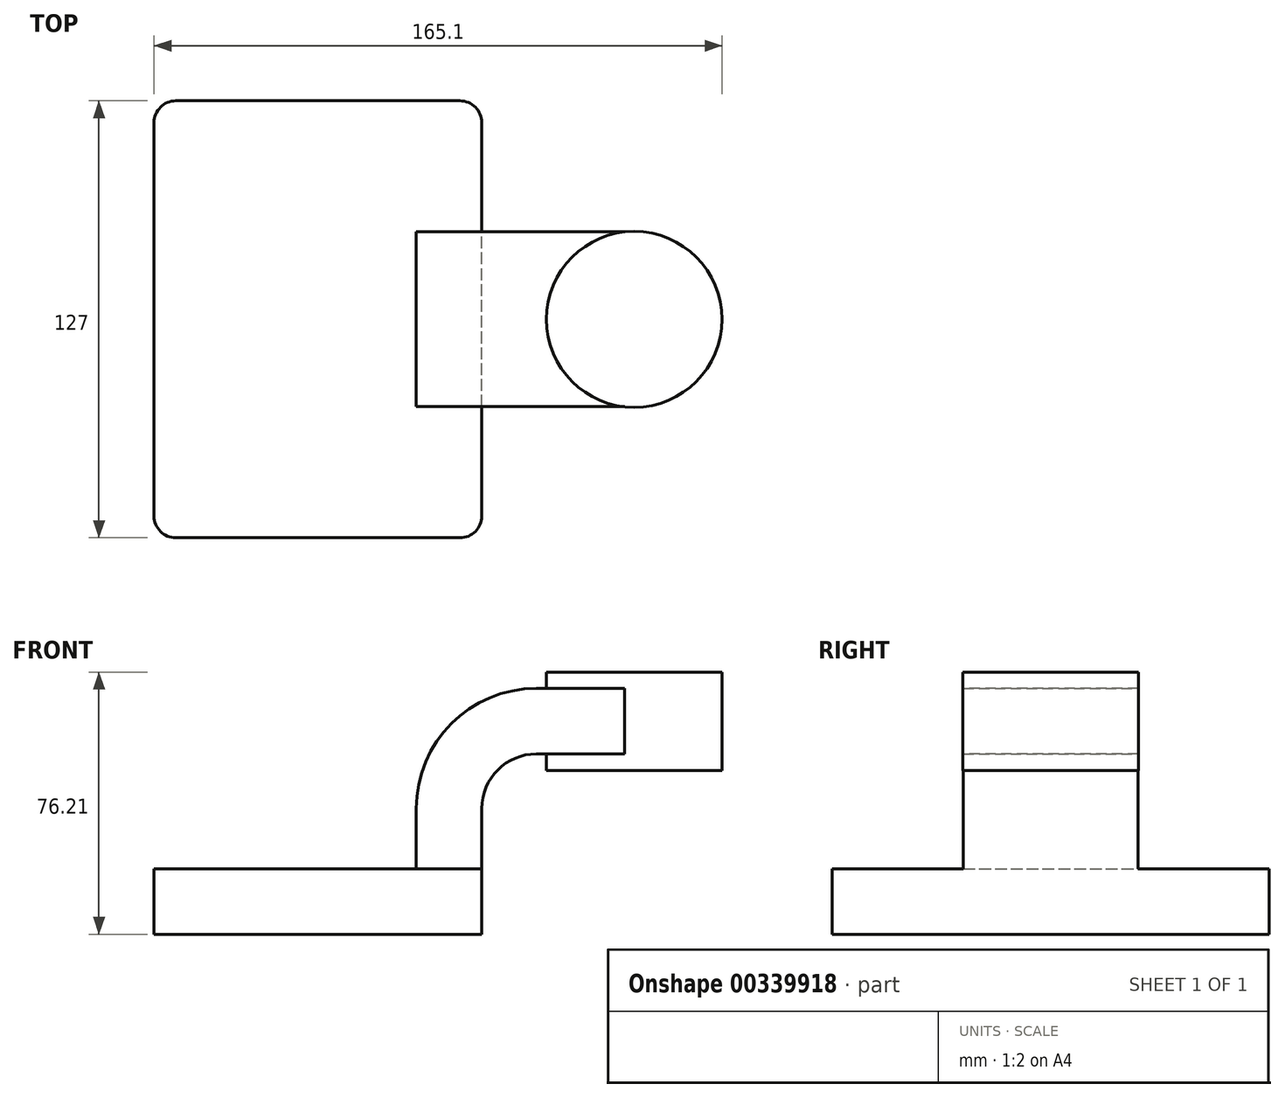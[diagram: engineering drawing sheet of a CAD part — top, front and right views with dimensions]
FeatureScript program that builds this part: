
annotation { "Feature Type Name" : "Feature", "Feature Type Description" : "" }
export const myFeature = defineFeature(function(context is Context, id is Id, definition is map)
    precondition{}
    {
        {
            var Q0;
            Q0=qCreatedBy(makeId("Front.planeOp"),FACE);
            var sketch = newSketch(context, id + "F0", { "sketchPlane" : qUnion([Q0])});
            skLineSegment(sketch, "E0.bottom", {"start": v(-47.63, 9.53) * mm, "end": v(47.63, 9.53) * mm});
            skLineSegment(sketch, "E0.top", {"start": v(-47.63, -9.53) * mm, "end": v(47.63, -9.53) * mm});
            skLineSegment(sketch, "E0.left", {"start": v(-47.63, 9.53) * mm, "end": v(-47.63, -9.53) * mm});
            skLineSegment(sketch, "E0.right", {"start": v(47.63, 9.53) * mm, "end": v(47.63, -9.53) * mm});
            skPoint(sketch, "E0.middle", {"position": v(0, 0) * mm});
            skLineSegment(sketch, "E1", {"start": v(47.63, 9.53) * mm, "end": v(47.63, 27) * mm});
            skArc(sketch, "E2", {"start": v(47.63, 27) * mm, "mid": v(52.27, 38.23) * mm, "end": v(63.5, 42.88) * mm});
            skLineSegment(sketch, "E3", {"start": v(63.5, 42.88) * mm, "end": v(91.92, 42.88) * mm});
            skLineSegment(sketch, "E4.bottom", {"start": v(117.47, 38.1) * mm, "end": v(66.67, 38.1) * mm});
            skLineSegment(sketch, "E4.top", {"start": v(117.47, 66.68) * mm, "end": v(66.67, 66.68) * mm});
            skLineSegment(sketch, "E4.left", {"start": v(117.47, 38.1) * mm, "end": v(117.47, 66.68) * mm});
            skLineSegment(sketch, "E4.right", {"start": v(66.67, 38.1) * mm, "end": v(66.67, 66.68) * mm});
            skPoint(sketch, "E4.middle", {"position": v(92.07, 52.39) * mm});
            skLineSegment(sketch, "E5.0", {"start": v(63.5, 61.93) * mm, "end": v(91.92, 61.93) * mm});
            skArc(sketch, "E5.1", {"start": v(28.58, 27) * mm, "mid": v(38.8, 51.7) * mm, "end": v(63.5, 61.93) * mm});
            skLineSegment(sketch, "E5.2", {"start": v(28.58, 9.53) * mm, "end": v(28.58, 27) * mm});
            skFitSpline(sketch, "E6", {"points": [v(-47.63, 9.53) * mm, v(63.5, 61.93) * mm], "startDerivative": vector(0, 71.57) * mm, "endDerivative": vector(190.5, 0) * mm});
            skLineSegment(sketch, "E7", {"start": v(91.92, 66.68) * mm, "end": v(91.92, 38.1) * mm});
            skSolve(sketch);
        }
        {
            var Q0;
            Q0=makeQuery(id+"F0.imprint","IMPRINT",FACE,{"disambiguationData":[TD([[makeQuery(id+"F0.imprint","IMPRINT",EDGE,{"derivedFrom":sQuery(id+"F0.wireOp",EDGE,"E0.top")}),1.0]])]});
            extrude(context, id + "F1", {"entities" : qUnion([Q0]), "endBound" : BoundingType.SYMMETRIC, "depth" : 127 * mm});
        }
        {
            var Q0;
            Q0=makeQuery(id+"F0.imprint","IMPRINT",FACE,{"disambiguationData":[TD([[makeQuery(id+"F0.imprint","IMPRINT",EDGE,{"derivedFrom":sQuery(id+"F0.wireOp",EDGE,"E5.1")}),1.0]])]});
            extrude(context, id + "F2", {"entities" : qUnion([Q0]), "operationType" : NewBodyOperationType.ADD, "endBound" : BoundingType.SYMMETRIC, "depth" : 15.88 * mm});
        }
        {
            var Q0;
            {var subQ4=sQuery(id+"F0.wireOp",EDGE,"E1");Q0=makeQuery(id+"F0.imprint","IMPRINT",FACE,{"disambiguationData":[TD([[makeQuery(id+"F0.imprint","IMPRINT",EDGE,{"derivedFrom":subQ4}),1.0]])]});}
            var Q1;
            {var subQ0=sQuery(id+"F0.wireOp",EDGE,"E7");var subQ1=sQuery(id+"F0.wireOp",EDGE,"E3");var subQ2=makeQuery(id+"F0.imprint","INTERSECT",VERTEX,{"derivedFrom":[subQ1,subQ0]});Q1=makeQuery(id+"F0.imprint","IMPRINT",FACE,{"disambiguationData":[TD([[makeQuery(id+"F0.imprint","IMPRINT",EDGE,{"disambiguationData":[TD([[subQ2,1.0]])],"derivedFrom":subQ1}),1.0]])]});}
            extrude(context, id + "F3", {"entities" : qUnion([Q0, Q1]), "operationType" : NewBodyOperationType.ADD, "endBound" : BoundingType.SYMMETRIC, "depth" : 50.8 * mm});
        }
        {
            var Q0;
            {var subQ4=sQuery(id+"F0.wireOp",EDGE,"E4.left");Q0=makeQuery(id+"F0.imprint","IMPRINT",FACE,{"disambiguationData":[TD([[makeQuery(id+"F0.imprint","IMPRINT",EDGE,{"derivedFrom":subQ4}),1.0]])]});}
            var Q1;
            Q1=sQuery(id+"F0.wireOp",EDGE,"E7");
            revolve(context, id + "F4", {"operationType" : NewBodyOperationType.ADD, "entities" : qUnion([Q0]), "axis" : qUnion([Q1]), "revolveType" : RevolveType.FULL});
        }
        {
            var Q0;
            Q0=makeQuery(id+"F1.opExtrude","CAP_EDGE",EDGE,{"disambiguationData":[OSD([sQuery(id+"F0.wireOp",EDGE,"E0.right")])],"isStart":false});
            var Q1;
            Q1=makeQuery(id+"F1.opExtrude","CAP_EDGE",EDGE,{"disambiguationData":[OSD([sQuery(id+"F0.wireOp",EDGE,"E0.left")])],"isStart":false});
            var Q2;
            Q2=makeQuery(id+"F1.opExtrude","CAP_EDGE",EDGE,{"disambiguationData":[OSD([sQuery(id+"F0.wireOp",EDGE,"E0.left")])],"isStart":true});
            var Q3;
            Q3=makeQuery(id+"F1.opExtrude","CAP_EDGE",EDGE,{"disambiguationData":[OSD([sQuery(id+"F0.wireOp",EDGE,"E0.right")])],"isStart":true});
            fillet(context, id + "F5", {"entities" : qUnion([Q0, Q1, Q2, Q3]), "radius" : 6.35 * mm, "tangentPropagation" : true, "allowEdgeOverflow" : false});
        }
    });
